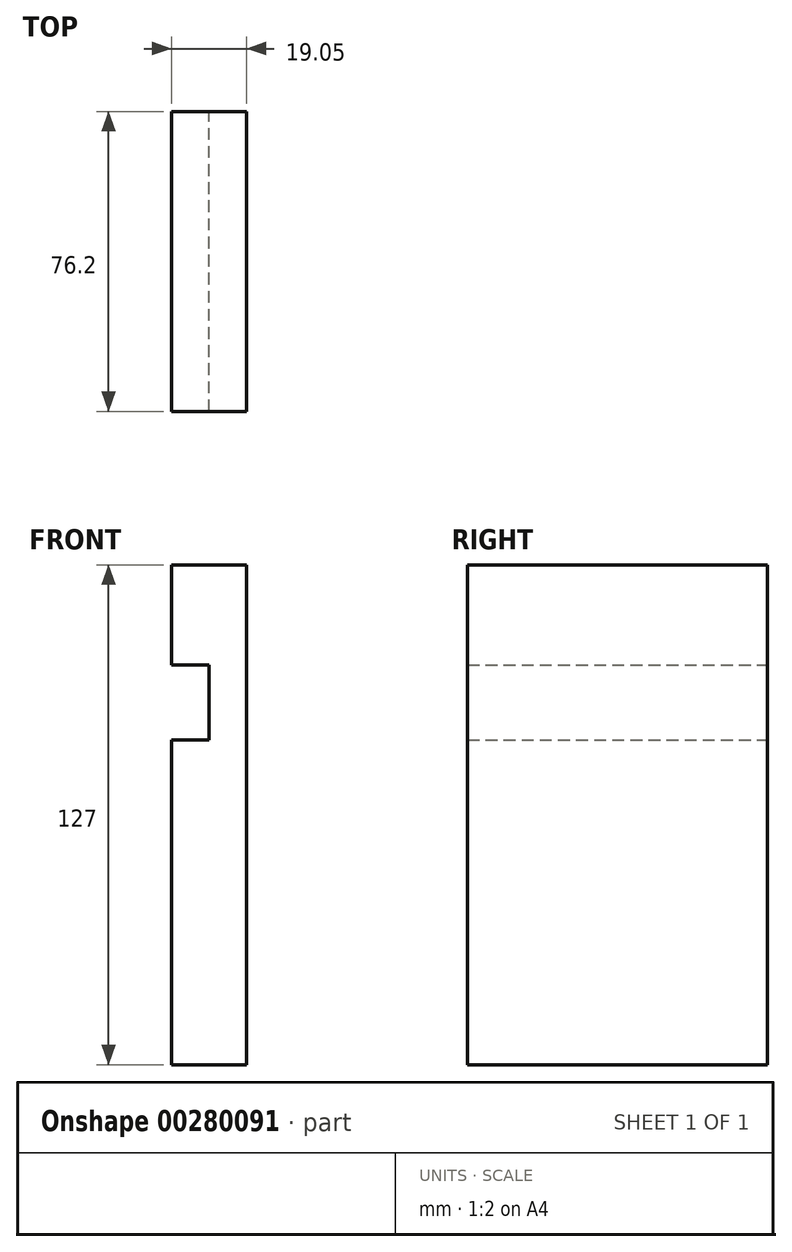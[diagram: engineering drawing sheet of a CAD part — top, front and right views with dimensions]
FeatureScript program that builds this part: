
annotation { "Feature Type Name" : "Feature", "Feature Type Description" : "" }
export const myFeature = defineFeature(function(context is Context, id is Id, definition is map)
    precondition{}
    {
        {
            var Q0;
            Q0=qCreatedBy(makeId("Front.planeOp"),FACE);
            var sketch = newSketch(context, id + "F0", { "sketchPlane" : qUnion([Q0])});
            skLineSegment(sketch, "E0", {"start": v(0, 0) * mm, "end": v(0, 127) * mm});
            skLineSegment(sketch, "E1", {"start": v(0, 127) * mm, "end": v(-19.05, 127) * mm});
            skLineSegment(sketch, "E2", {"start": v(-19.05, 127) * mm, "end": v(-19.05, 101.6) * mm});
            skLineSegment(sketch, "E3", {"start": v(-19.05, 101.6) * mm, "end": v(-9.52, 101.6) * mm});
            skLineSegment(sketch, "E4", {"start": v(-9.52, 101.6) * mm, "end": v(-9.52, 82.55) * mm});
            skLineSegment(sketch, "E5", {"start": v(-9.52, 82.55) * mm, "end": v(-19.05, 82.55) * mm});
            skLineSegment(sketch, "E6", {"start": v(-19.05, 82.55) * mm, "end": v(-19.05, 0) * mm});
            skLineSegment(sketch, "E7", {"start": v(-19.05, 0) * mm, "end": v(0, 0) * mm});
            skSolve(sketch);
        }
        {
            var Q0;
            Q0 = qSketchRegion(id + "F0", true);
            extrude(context, id + "F1", {"entities" : qUnion([Q0]), "depth" : 76.2 * mm});
        }
    });
